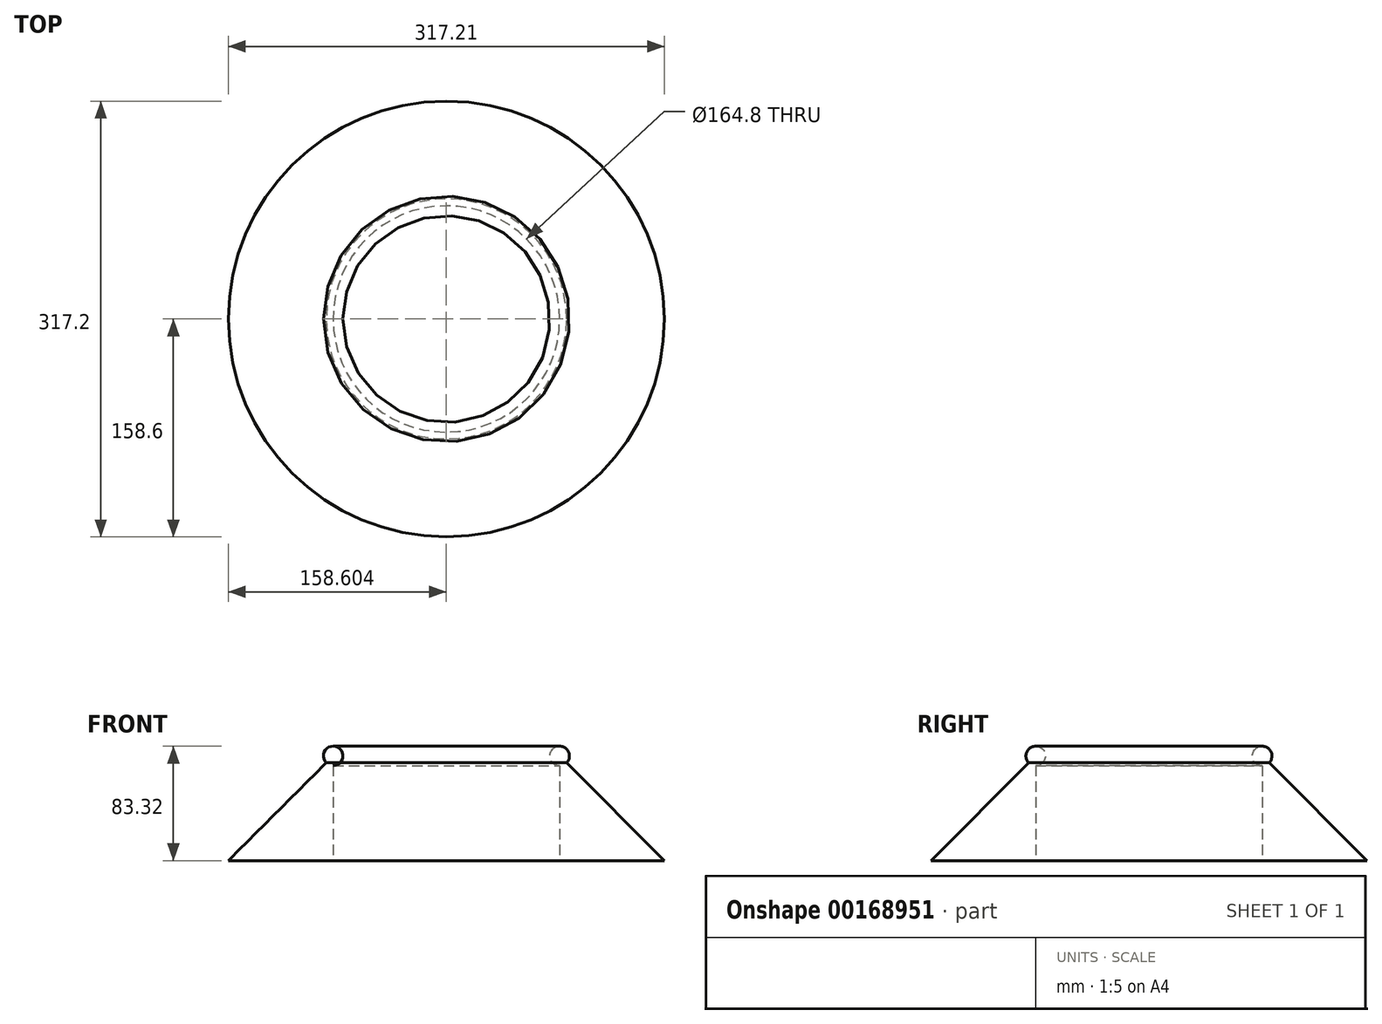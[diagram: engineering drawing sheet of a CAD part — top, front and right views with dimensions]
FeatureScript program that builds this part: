
annotation { "Feature Type Name" : "Feature", "Feature Type Description" : "" }
export const myFeature = defineFeature(function(context is Context, id is Id, definition is map)
    precondition{}
    {
        {
            var Q0;
            Q0=qCreatedBy(makeId("Front.planeOp"),FACE);
            var sketch = newSketch(context, id + "F0", { "sketchPlane" : qUnion([Q0])});
            skLineSegment(sketch, "E0", {"start": v(-115.4, -39.12) * mm, "end": v(-39.2, 37.08) * mm});
            skLineSegment(sketch, "E1", {"start": v(-39.2, 37.08) * mm, "end": v(-39.2, -39.12) * mm});
            skLineSegment(sketch, "E2", {"start": v(-39.2, -39.12) * mm, "end": v(-115.4, -39.12) * mm});
            skCircle(sketch, "E3", {"center": v(-39.2, 37.08) * mm, "radius": 7.11 * mm});
            skLineSegment(sketch, "E4", {"start": v(43.2, -48.04) * mm, "end": v(43.2, 61.25) * mm, "construction": true});
            skCircle(sketch, "E5", {"center": v(-115.8, 28.8) * mm, "radius": 19.52 * mm, "construction": true});
            skCircle(sketch, "E6", {"center": v(-39.2, 37.08) * mm, "radius": 6.35 * mm, "construction": true});
            skSolve(sketch);
        }
        {
            var Q0;
            {var subQ0=sQuery(id+"F0.wireOp",EDGE,"E1");var subQ1=sQuery(id+"F0.wireOp",EDGE,"E0");var subQ2=makeQuery(id+"F0.imprint","INTERSECT",VERTEX,{"derivedFrom":[subQ1,subQ0]});Q0=makeQuery(id+"F0.imprint","IMPRINT",FACE,{"disambiguationData":[TD([[makeQuery(id+"F0.imprint","IMPRINT",EDGE,{"disambiguationData":[TD([[subQ2,1.0]])],"derivedFrom":subQ1}),1.0]])]});}
            var Q1;
            {var subQ0=sQuery(id+"F0.wireOp",EDGE,"E1");var subQ1=sQuery(id+"F0.wireOp",EDGE,"E0");var subQ2=makeQuery(id+"F0.imprint","INTERSECT",VERTEX,{"derivedFrom":[subQ1,subQ0]});Q1=makeQuery(id+"F0.imprint","IMPRINT",FACE,{"disambiguationData":[TD([[makeQuery(id+"F0.imprint","IMPRINT",EDGE,{"disambiguationData":[TD([[subQ2,1.0]])],"derivedFrom":subQ1}),-1.0]])]});}
            var Q2;
            {var subQ0=sQuery(id+"F0.wireOp",EDGE,"E2");Q2=makeQuery(id+"F0.imprint","IMPRINT",FACE,{"disambiguationData":[TD([[makeQuery(id+"F0.imprint","IMPRINT",EDGE,{"derivedFrom":subQ0}),-1.0]])]});}
            var Q3;
            Q3=sQuery(id+"F0.wireOp",EDGE,"E4");
            revolve(context, id + "F1", {"entities" : qUnion([Q0, Q1, Q2]), "axis" : qUnion([Q3]), "revolveType" : RevolveType.FULL});
        }
    });
